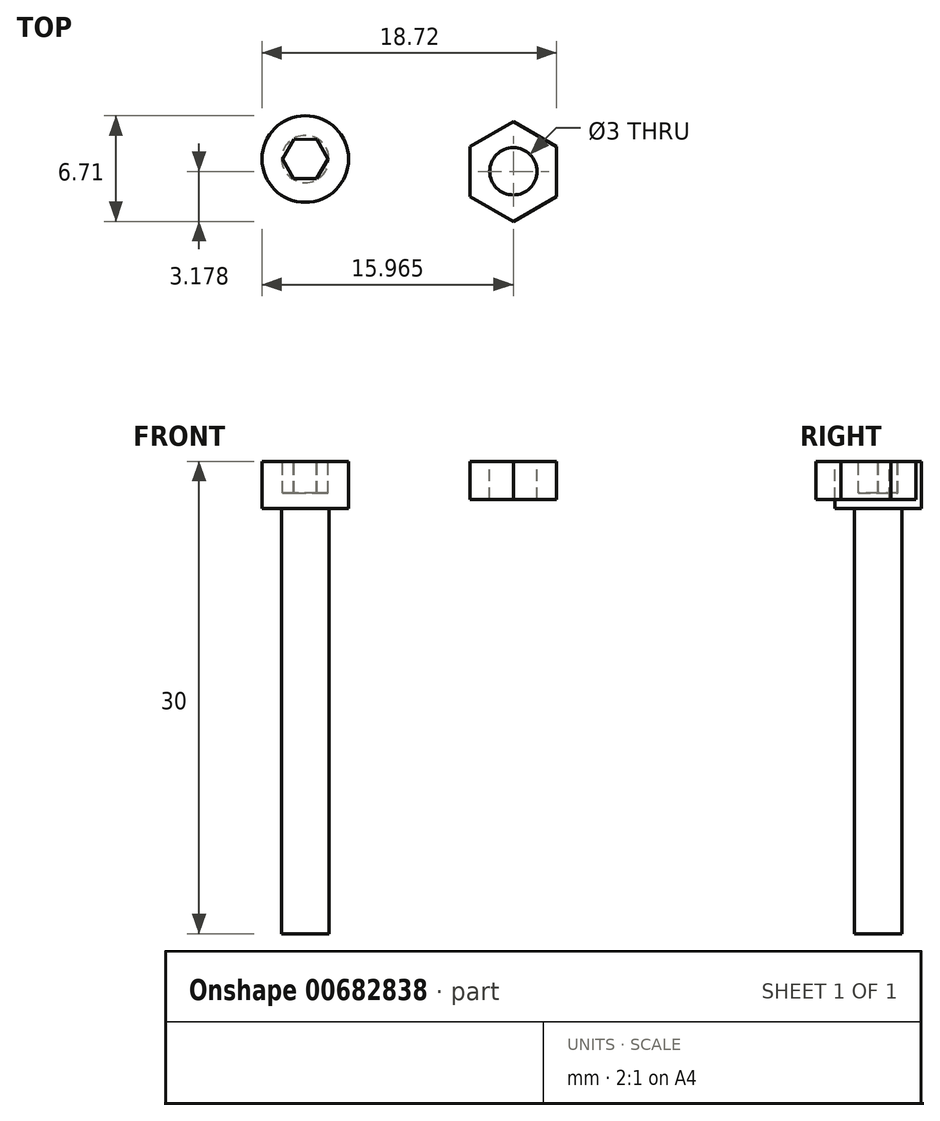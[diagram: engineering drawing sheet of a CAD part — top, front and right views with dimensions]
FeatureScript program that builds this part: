
annotation { "Feature Type Name" : "Feature", "Feature Type Description" : "" }
export const myFeature = defineFeature(function(context is Context, id is Id, definition is map)
    precondition{}
    {
        {
            var Q0;
            Q0=qCreatedBy(makeId("Top.planeOp"),FACE);
            var sketch = newSketch(context, id + "F0", { "sketchPlane" : qUnion([Q0])});
            skCircle(sketch, "E0", {"center": v(0, 0) * mm, "radius": 2.75 * mm});
            skSolve(sketch);
        }
        {
            var Q0;
            Q0=qCreatedBy(makeId("Top.planeOp"),FACE);
            var sketch = newSketch(context, id + "F1", { "sketchPlane" : qUnion([Q0])});
            skCircle(sketch, "E1", {"center": v(0, 0) * mm, "radius": 1.5 * mm});
            skSolve(sketch);
        }
        {
            var Q0;
            Q0=qCreatedBy(makeId("Top.planeOp"),FACE);
            var sketch = newSketch(context, id + "F2", { "sketchPlane" : qUnion([Q0])});
            skCircle(sketch, "E2.cCircle", {"center": v(0, 0) * mm, "radius": 1.25 * mm, "construction": true});
            skLineSegment(sketch, "E2.0", {"start": v(-1.44, 0.01) * mm, "end": v(-0.71, 1.26) * mm});
            skLineSegment(sketch, "E2.1", {"start": v(-0.71, 1.26) * mm, "end": v(0.73, 1.24) * mm});
            skLineSegment(sketch, "E2.2", {"start": v(0.73, 1.24) * mm, "end": v(1.44, -0.01) * mm});
            skLineSegment(sketch, "E2.3", {"start": v(1.44, -0.01) * mm, "end": v(0.71, -1.26) * mm});
            skLineSegment(sketch, "E2.4", {"start": v(0.71, -1.26) * mm, "end": v(-0.73, -1.24) * mm});
            skLineSegment(sketch, "E2.5", {"start": v(-0.73, -1.24) * mm, "end": v(-1.44, 0.01) * mm});
            skPoint(sketch, "E2.0.midPoint", {"position": v(-1.08, 0.63) * mm});
            skSolve(sketch);
        }
        {
            var Q0;
            Q0 = qSketchRegion(id + "F0", true);
            extrude(context, id + "F3", {"entities" : qUnion([Q0]), "oppositeDirection" : true, "depth" : 3 * mm, "offsetDistance" : 25 * mm});
        }
        {
            var Q0;
            Q0 = qSketchRegion(id + "F1", true);
            extrude(context, id + "F4", {"entities" : qUnion([Q0]), "operationType" : NewBodyOperationType.ADD, "oppositeDirection" : true, "depth" : 30 * mm, "offsetDistance" : 25 * mm});
        }
        {
            var Q0;
            Q0 = qSketchRegion(id + "F2", true);
            extrude(context, id + "F5", {"entities" : qUnion([Q0]), "operationType" : NewBodyOperationType.REMOVE, "oppositeDirection" : true, "depth" : 2 * mm, "offsetDistance" : 25 * mm});
        }
        {
            var Q0;
            Q0=qCreatedBy(makeId("Top.planeOp"),FACE);
            var sketch = newSketch(context, id + "F6", { "sketchPlane" : qUnion([Q0])});
            skCircle(sketch, "E3", {"center": v(13.22, -0.78) * mm, "radius": 1.5 * mm});
            skCircle(sketch, "E4.cCircle", {"center": v(13.22, -0.78) * mm, "radius": 2.75 * mm, "construction": true});
            skLineSegment(sketch, "E4.0", {"start": v(10.47, -2.37) * mm, "end": v(10.47, 0.8) * mm});
            skLineSegment(sketch, "E4.1", {"start": v(10.47, 0.8) * mm, "end": v(13.22, 2.4) * mm});
            skLineSegment(sketch, "E4.2", {"start": v(13.22, 2.4) * mm, "end": v(15.97, 0.8) * mm});
            skLineSegment(sketch, "E4.3", {"start": v(15.97, 0.8) * mm, "end": v(15.97, -2.37) * mm});
            skLineSegment(sketch, "E4.4", {"start": v(15.97, -2.37) * mm, "end": v(13.22, -3.96) * mm});
            skLineSegment(sketch, "E4.5", {"start": v(13.22, -3.96) * mm, "end": v(10.47, -2.37) * mm});
            skPoint(sketch, "E4.0.midPoint", {"position": v(10.47, -0.78) * mm});
            skSolve(sketch);
        }
        {
            var Q0;
            Q0=makeQuery(id+"F6.imprint","IMPRINT",FACE,{"disambiguationData":[TD([[makeQuery(id+"F6.imprint","IMPRINT",EDGE,{"derivedFrom":sQuery(id+"F6.wireOp",EDGE,"E3")}),-1.0]])]});
            var Q1;
            Q1=sQuery(id+"F6.wireOp",EDGE,"E3");
            var Q2;
            Q2=sQuery(id+"F6.wireOp",EDGE,"E4.1");
            var Q3;
            Q3=sQuery(id+"F6.wireOp",EDGE,"E4.0");
            var Q4;
            Q4=sQuery(id+"F6.wireOp",EDGE,"E4.5");
            var Q5;
            Q5=sQuery(id+"F6.wireOp",EDGE,"E4.4");
            var Q6;
            Q6=sQuery(id+"F6.wireOp",EDGE,"E4.3");
            var Q7;
            Q7=sQuery(id+"F6.wireOp",EDGE,"E4.2");
            extrude(context, id + "F7", {"entities" : qUnion([Q0]), "surfaceEntities" : qUnion([Q1, Q2, Q3, Q4, Q5, Q6, Q7]), "oppositeDirection" : true, "depth" : 2.4 * mm, "offsetDistance" : 25 * mm});
        }
    });
